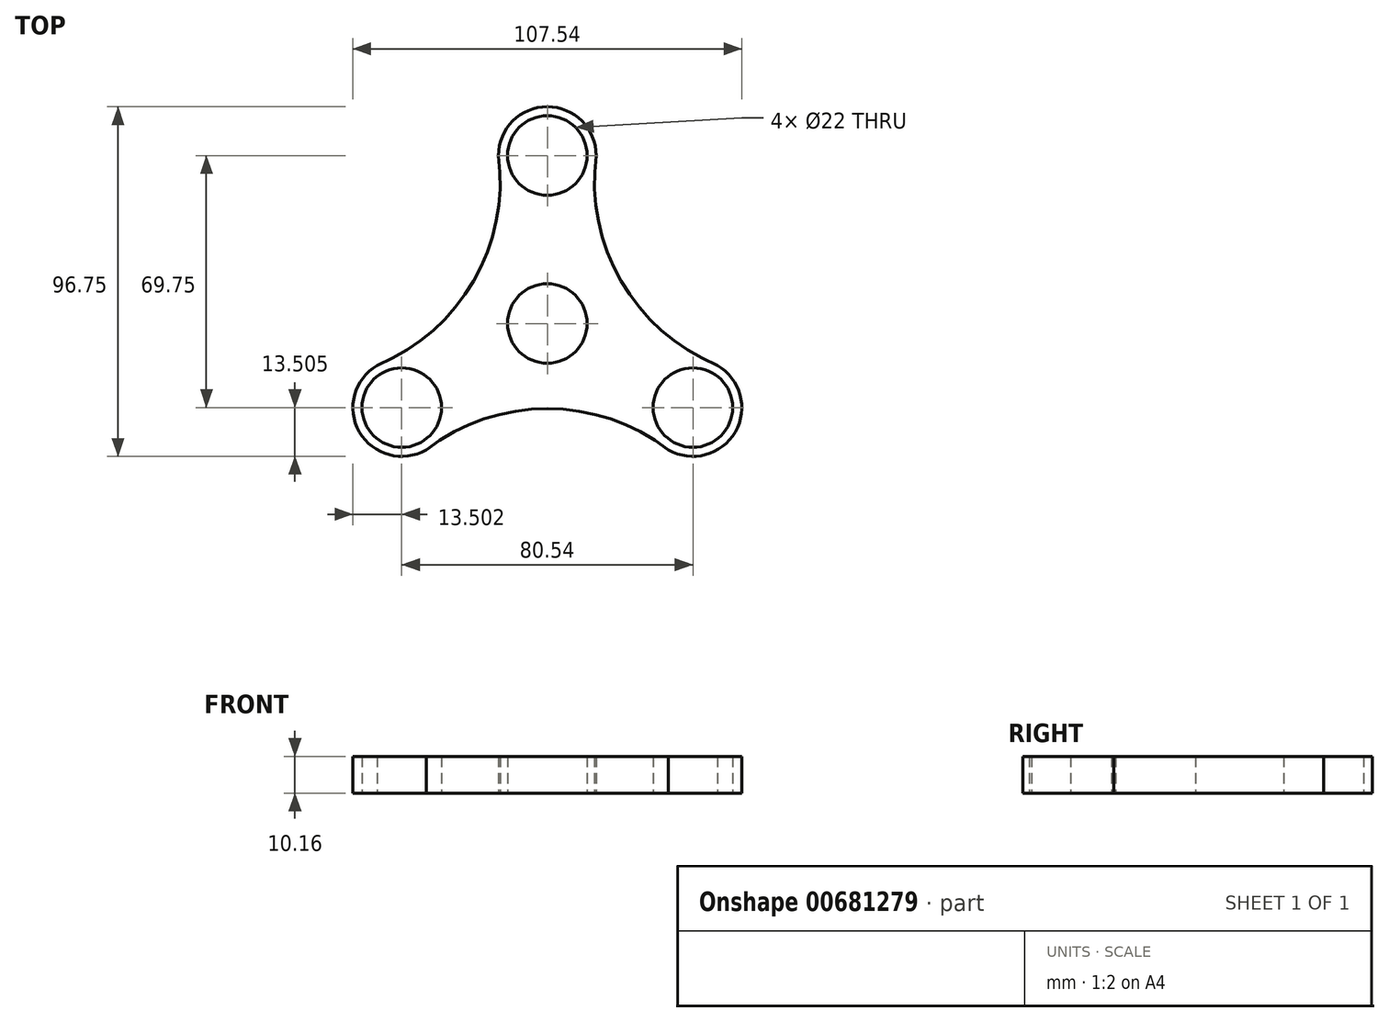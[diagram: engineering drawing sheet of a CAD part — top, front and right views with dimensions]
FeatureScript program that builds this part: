
annotation { "Feature Type Name" : "Feature", "Feature Type Description" : "" }
export const myFeature = defineFeature(function(context is Context, id is Id, definition is map)
    precondition{}
    {
        {
            var Q0;
            Q0=qCreatedBy(makeId("Top.planeOp"),FACE);
            var sketch = newSketch(context, id + "F0", { "sketchPlane" : qUnion([Q0])});
            skCircle(sketch, "E0", {"center": v(-56.66, 34.11) * mm, "radius": 11 * mm});
            skLineSegment(sketch, "E1", {"start": v(-56.66, 34.11) * mm, "end": v(-56.66, 94.11) * mm});
            skLineSegment(sketch, "E2", {"start": v(-56.66, 34.11) * mm, "end": v(-4.7, 4.11) * mm});
            skLineSegment(sketch, "E3", {"start": v(-56.66, 34.11) * mm, "end": v(-108.62, 4.11) * mm});
            skCircle(sketch, "E4", {"center": v(-56.66, 80.61) * mm, "radius": 13.5 * mm});
            skCircle(sketch, "E5", {"center": v(-96.93, 10.86) * mm, "radius": 13.5 * mm});
            skCircle(sketch, "E6", {"center": v(-16.39, 10.86) * mm, "radius": 13.5 * mm});
            skArc(sketch, "E7", {"start": v(-103.68, 22.56) * mm, "mid": v(-77.05, 45.89) * mm, "end": v(-70.16, 80.61) * mm});
            skArc(sketch, "E8", {"start": v(-43.16, 80.61) * mm, "mid": v(-36.27, 45.89) * mm, "end": v(-9.64, 22.56) * mm});
            skArc(sketch, "E9", {"start": v(-23.14, -0.83) * mm, "mid": v(-56.66, 10.57) * mm, "end": v(-90.18, -0.83) * mm});
            skCircle(sketch, "E10", {"center": v(-96.93, 10.86) * mm, "radius": 11 * mm});
            skCircle(sketch, "E11", {"center": v(-16.39, 10.86) * mm, "radius": 11 * mm});
            skCircle(sketch, "E12", {"center": v(-56.66, 80.61) * mm, "radius": 11 * mm});
            skSolve(sketch);
        }
        {
            var Q0;
            {var subQ1=sQuery(id+"F0.wireOp",EDGE,"E0");var subQ7=sQuery(id+"F0.wireOp",EDGE,"E1");var subQ8=makeQuery(id+"F0.imprint","INTERSECT",VERTEX,{"derivedFrom":[subQ1,subQ7]});Q0=makeQuery(id+"F0.imprint","IMPRINT",FACE,{"disambiguationData":[TD([[makeQuery(id+"F0.imprint","IMPRINT",EDGE,{"disambiguationData":[TD([[subQ8,1.0]])],"derivedFrom":subQ1}),-1.0]])]});}
            var Q1;
            {var subQ5=sQuery(id+"F0.wireOp",EDGE,"E3");var subQ6=sQuery(id+"F0.wireOp",EDGE,"E0");var subQ7=makeQuery(id+"F0.imprint","INTERSECT",VERTEX,{"derivedFrom":[subQ6,subQ5]});Q1=makeQuery(id+"F0.imprint","IMPRINT",FACE,{"disambiguationData":[TD([[makeQuery(id+"F0.imprint","IMPRINT",EDGE,{"disambiguationData":[TD([[subQ7,1.0]])],"derivedFrom":subQ6}),-1.0]])]});}
            var Q2;
            {var subQ3=sQuery(id+"F0.wireOp",EDGE,"E3");var subQ5=sQuery(id+"F0.wireOp",EDGE,"E0");var subQ6=makeQuery(id+"F0.imprint","INTERSECT",VERTEX,{"derivedFrom":[subQ5,subQ3]});Q2=makeQuery(id+"F0.imprint","IMPRINT",FACE,{"disambiguationData":[TD([[makeQuery(id+"F0.imprint","IMPRINT",EDGE,{"disambiguationData":[TD([[subQ6,-1.0]])],"derivedFrom":subQ5}),-1.0]])]});}
            var Q3;
            {var subQ0=sQuery(id+"F0.wireOp",EDGE,"E6");var subQ1=sQuery(id+"F0.wireOp",EDGE,"E2");var subQ8=makeQuery(id+"F0.imprint","INTERSECT",VERTEX,{"disambiguationData":[OD(1.0)],"derivedFrom":[subQ1,subQ0]});Q3=makeQuery(id+"F0.imprint","IMPRINT",FACE,{"disambiguationData":[TD([[makeQuery(id+"F0.imprint","IMPRINT",EDGE,{"disambiguationData":[TD([[subQ8,-1.0]])],"derivedFrom":subQ1}),-1.0]])]});}
            var Q4;
            {var subQ1=sQuery(id+"F0.wireOp",EDGE,"E6");var subQ3=sQuery(id+"F0.wireOp",EDGE,"E2");var subQ4=makeQuery(id+"F0.imprint","INTERSECT",VERTEX,{"disambiguationData":[OD(1.0)],"derivedFrom":[subQ3,subQ1]});Q4=makeQuery(id+"F0.imprint","IMPRINT",FACE,{"disambiguationData":[TD([[makeQuery(id+"F0.imprint","IMPRINT",EDGE,{"disambiguationData":[TD([[subQ4,-1.0]])],"derivedFrom":subQ3}),1.0]])]});}
            var Q5;
            {var subQ1=sQuery(id+"F0.wireOp",EDGE,"E5");var subQ3=sQuery(id+"F0.wireOp",EDGE,"E3");var subQ4=makeQuery(id+"F0.imprint","INTERSECT",VERTEX,{"disambiguationData":[OD(1.0)],"derivedFrom":[subQ3,subQ1]});Q5=makeQuery(id+"F0.imprint","IMPRINT",FACE,{"disambiguationData":[TD([[makeQuery(id+"F0.imprint","IMPRINT",EDGE,{"disambiguationData":[TD([[subQ4,-1.0]])],"derivedFrom":subQ3}),1.0]])]});}
            var Q6;
            {var subQ0=sQuery(id+"F0.wireOp",EDGE,"E5");var subQ1=sQuery(id+"F0.wireOp",EDGE,"E3");var subQ5=makeQuery(id+"F0.imprint","INTERSECT",VERTEX,{"disambiguationData":[OD(1.0)],"derivedFrom":[subQ1,subQ0]});Q6=makeQuery(id+"F0.imprint","IMPRINT",FACE,{"disambiguationData":[TD([[makeQuery(id+"F0.imprint","IMPRINT",EDGE,{"disambiguationData":[TD([[subQ5,-1.0]])],"derivedFrom":subQ1}),-1.0]])]});}
            var Q7;
            {var subQ0=sQuery(id+"F0.wireOp",EDGE,"E4");var subQ1=sQuery(id+"F0.wireOp",EDGE,"E1");var subQ8=makeQuery(id+"F0.imprint","INTERSECT",VERTEX,{"disambiguationData":[OD(1.0)],"derivedFrom":[subQ1,subQ0]});Q7=makeQuery(id+"F0.imprint","IMPRINT",FACE,{"disambiguationData":[TD([[makeQuery(id+"F0.imprint","IMPRINT",EDGE,{"disambiguationData":[TD([[subQ8,-1.0]])],"derivedFrom":subQ1}),-1.0]])]});}
            var Q8;
            {var subQ1=sQuery(id+"F0.wireOp",EDGE,"E4");var subQ3=sQuery(id+"F0.wireOp",EDGE,"E1");var subQ4=makeQuery(id+"F0.imprint","INTERSECT",VERTEX,{"disambiguationData":[OD(1.0)],"derivedFrom":[subQ3,subQ1]});Q8=makeQuery(id+"F0.imprint","IMPRINT",FACE,{"disambiguationData":[TD([[makeQuery(id+"F0.imprint","IMPRINT",EDGE,{"disambiguationData":[TD([[subQ4,-1.0]])],"derivedFrom":subQ3}),1.0]])]});}
            extrude(context, id + "F1", {"entities" : qUnion([Q0, Q1, Q2, Q3, Q4, Q5, Q6, Q7, Q8]), "depth" : 10.16 * mm, "offsetDistance" : 25 * mm});
        }
    });
